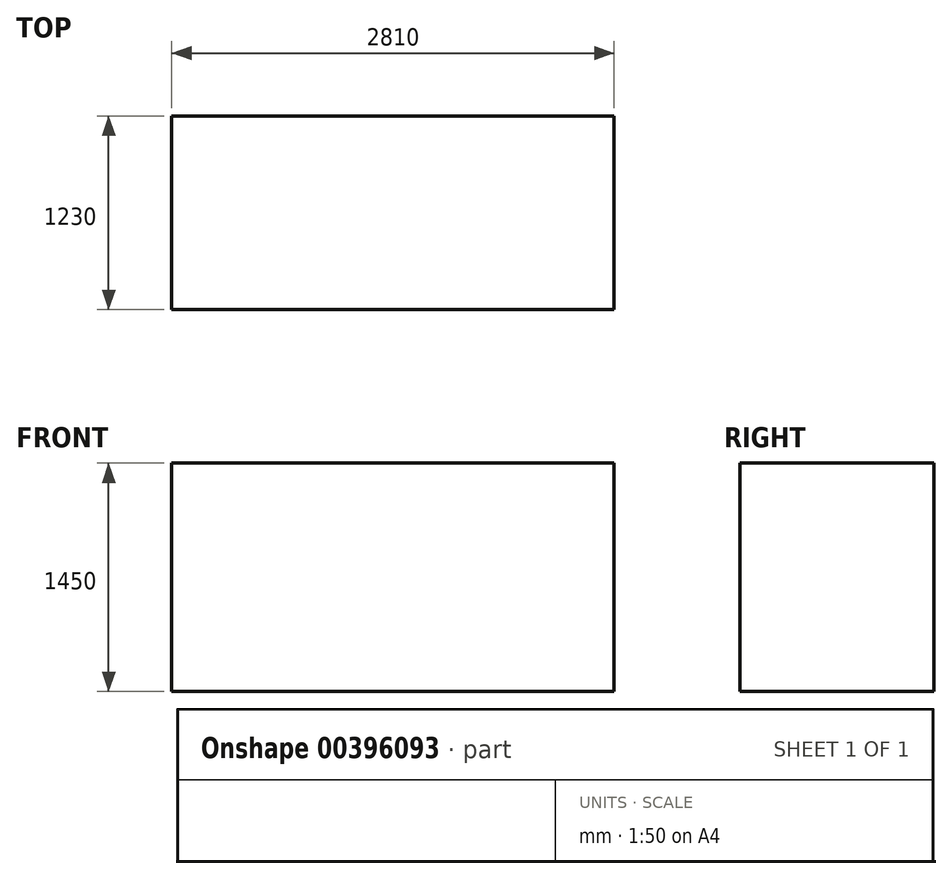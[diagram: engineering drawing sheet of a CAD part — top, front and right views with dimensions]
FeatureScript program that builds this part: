
annotation { "Feature Type Name" : "Feature", "Feature Type Description" : "" }
export const myFeature = defineFeature(function(context is Context, id is Id, definition is map)
    precondition{}
    {
        {
            var Q0;
            Q0=qCreatedBy(makeId("Top.planeOp"),FACE);
            var sketch = newSketch(context, id + "F0", { "sketchPlane" : qUnion([Q0])});
            skLineSegment(sketch, "E0.bottom", {"start": v(0, 0) * mm, "end": v(2810, 0) * mm});
            skLineSegment(sketch, "E0.top", {"start": v(0, 1230) * mm, "end": v(2810, 1230) * mm});
            skLineSegment(sketch, "E0.left", {"start": v(0, 0) * mm, "end": v(0, 1230) * mm});
            skLineSegment(sketch, "E0.right", {"start": v(2810, 0) * mm, "end": v(2810, 1230) * mm});
            skSolve(sketch);
        }
        {
            var Q0;
            Q0=makeQuery(id+"F0.imprint","IMPRINT",FACE,{"disambiguationData":[TD([[makeQuery(id+"F0.imprint","IMPRINT",EDGE,{"derivedFrom":sQuery(id+"F0.wireOp",EDGE,"E0.bottom")}),1.0]])]});
            extrude(context, id + "F1", {"entities" : qUnion([Q0]), "depth" : 1450 * mm, "offsetDistance" : 25 * mm});
        }
    });
